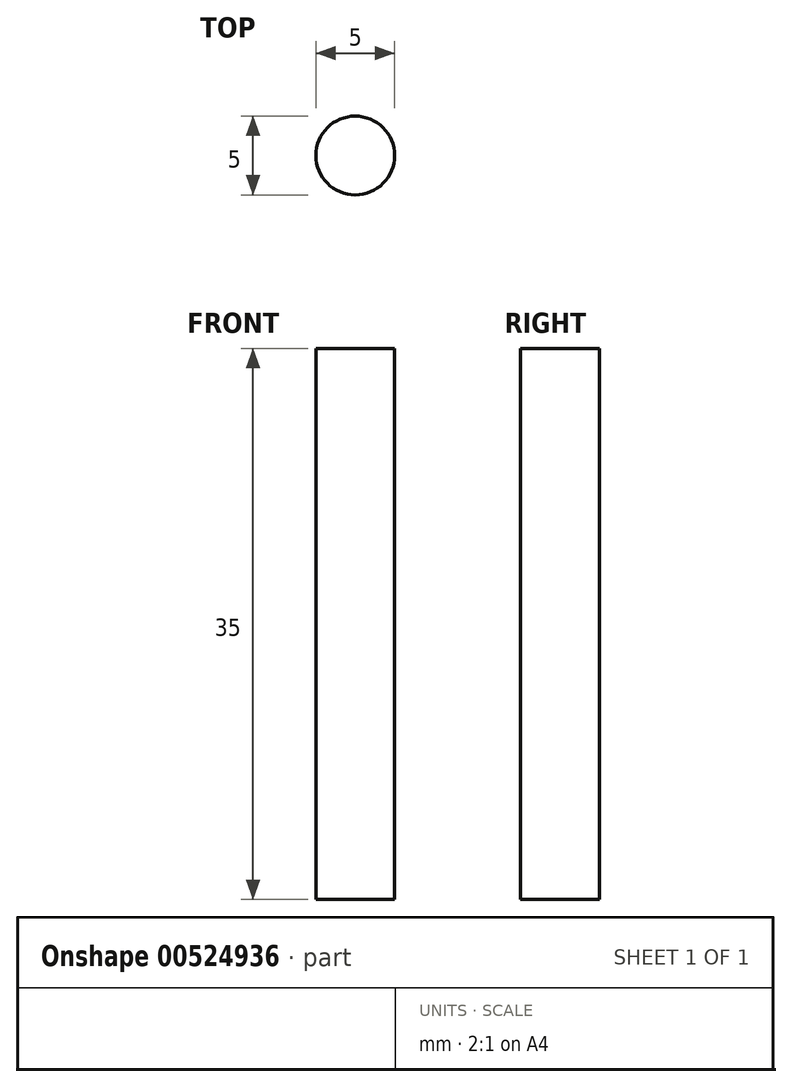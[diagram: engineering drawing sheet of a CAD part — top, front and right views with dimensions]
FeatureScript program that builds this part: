
annotation { "Feature Type Name" : "Feature", "Feature Type Description" : "" }
export const myFeature = defineFeature(function(context is Context, id is Id, definition is map)
    precondition{}
    {
        {
            var Q0;
            Q0=qCreatedBy(makeId("Top.planeOp"),FACE);
            var sketch = newSketch(context, id + "F0", { "sketchPlane" : qUnion([Q0])});
            skCircle(sketch, "E0", {"center": v(0, 0) * mm, "radius": 2.5 * mm});
            skSolve(sketch);
        }
        {
            var Q0;
            Q0 = qSketchRegion(id + "F0", true);
            extrude(context, id + "F1", {"entities" : qUnion([Q0]), "depth" : 35 * mm, "offsetDistance" : 25 * mm});
        }
    });
